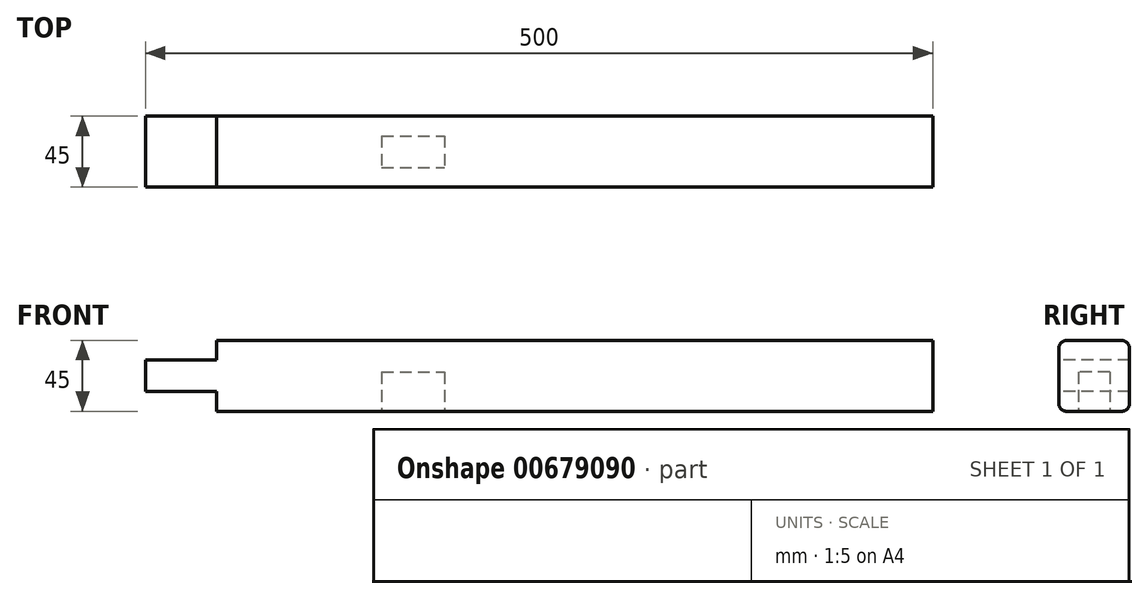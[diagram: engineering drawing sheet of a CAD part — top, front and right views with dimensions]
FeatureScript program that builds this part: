
annotation { "Feature Type Name" : "Feature", "Feature Type Description" : "" }
export const myFeature = defineFeature(function(context is Context, id is Id, definition is map)
    precondition{}
    {
        {
            var Q0;
            Q0=qCreatedBy(makeId("Right.planeOp"),FACE);
            var sketch = newSketch(context, id + "F0", { "sketchPlane" : qUnion([Q0])});
            skLineSegment(sketch, "E0.bottom", {"start": v(0, 0) * mm, "end": v(45, 0) * mm});
            skLineSegment(sketch, "E0.top", {"start": v(0, 45) * mm, "end": v(45, 45) * mm});
            skLineSegment(sketch, "E0.left", {"start": v(0, 0) * mm, "end": v(0, 45) * mm});
            skLineSegment(sketch, "E0.right", {"start": v(45, 0) * mm, "end": v(45, 45) * mm});
            skSolve(sketch);
        }
        {
            var Q0;
            Q0=qSketchRegion(id+"F0",true);
            extrude(context, id + "F1", {"entities" : qUnion([Q0]), "endBound" : BoundingType.SYMMETRIC, "depth" : 500 * mm, "offsetDistance" : 25 * mm});
        }
        {
            var Q0;
            Q0=makeQuery(id+"F1.opExtrude","SWEPT_EDGE",EDGE,{"disambiguationData":[OSD([sQuery(id+"F0.wireOp",EDGE,"E0.top"),sQuery(id+"F0.wireOp",EDGE,"E0.left")])]});
            var Q1;
            Q1=makeQuery(id+"F1.opExtrude","SWEPT_EDGE",EDGE,{"disambiguationData":[OSD([sQuery(id+"F0.wireOp",EDGE,"E0.top"),sQuery(id+"F0.wireOp",EDGE,"E0.right")])]});
            var Q2;
            Q2=makeQuery(id+"F1.opExtrude","SWEPT_EDGE",EDGE,{"disambiguationData":[OSD([sQuery(id+"F0.wireOp",EDGE,"E0.bottom"),sQuery(id+"F0.wireOp",EDGE,"E0.left")])]});
            var Q3;
            Q3=makeQuery(id+"F1.opExtrude","SWEPT_EDGE",EDGE,{"disambiguationData":[OSD([sQuery(id+"F0.wireOp",EDGE,"E0.bottom"),sQuery(id+"F0.wireOp",EDGE,"E0.right")])]});
            fillet(context, id + "F2", {"entities" : qUnion([Q0, Q1, Q2, Q3]), "radius" : 5 * mm, "tangentPropagation" : true, "allowEdgeOverflow" : false});
        }
        {
            var Q0;
            Q0=makeQuery(id+"F1.opExtrude","SWEPT_FACE",FACE,{"disambiguationData":[OSD([sQuery(id+"F0.wireOp",EDGE,"E0.left")])]});
            var sketch = newSketch(context, id + "F3", { "sketchPlane" : qUnion([Q0])});
            skLineSegment(sketch, "E1", {"start": v(-250, 22.5) * mm, "end": v(-205, 22.5) * mm, "construction": true});
            skLineSegment(sketch, "E2.bottom", {"start": v(-205, 12.5) * mm, "end": v(-250, 12.5) * mm});
            skLineSegment(sketch, "E2.top", {"start": v(-205, 32.5) * mm, "end": v(-250, 32.5) * mm});
            skLineSegment(sketch, "E2.left", {"start": v(-205, 12.5) * mm, "end": v(-205, 32.5) * mm, "construction": true});
            skLineSegment(sketch, "E2.right", {"start": v(-250, 12.5) * mm, "end": v(-250, 32.5) * mm});
            skPoint(sketch, "E2.middle", {"position": v(-227.5, 22.5) * mm});
            skLineSegment(sketch, "E3.bottom", {"start": v(-250, 32.5) * mm, "end": v(-205, 32.5) * mm});
            skLineSegment(sketch, "E3.top", {"start": v(-250, 45) * mm, "end": v(-205, 45) * mm});
            skLineSegment(sketch, "E3.left", {"start": v(-250, 32.5) * mm, "end": v(-250, 45) * mm});
            skLineSegment(sketch, "E3.right", {"start": v(-205, 32.5) * mm, "end": v(-205, 45) * mm});
            skLineSegment(sketch, "E4.bottom", {"start": v(-250, 12.5) * mm, "end": v(-205, 12.5) * mm});
            skLineSegment(sketch, "E4.top", {"start": v(-250, 0) * mm, "end": v(-205, 0) * mm});
            skLineSegment(sketch, "E4.left", {"start": v(-250, 12.5) * mm, "end": v(-250, 0) * mm});
            skLineSegment(sketch, "E4.right", {"start": v(-205, 12.5) * mm, "end": v(-205, 0) * mm});
            skSolve(sketch);
        }
        {
            var Q0;
            Q0=qSketchRegion(id+"F3",true);
            extrude(context, id + "F4", {"entities" : qUnion([Q0]), "operationType" : NewBodyOperationType.REMOVE, "endBound" : BoundingType.THROUGH_ALL, "oppositeDirection" : true, "depth" : 25 * mm, "offsetDistance" : 25 * mm});
        }
        {
            var Q0;
            Q0=makeQuery(id+"F1.opExtrude","CAP_FACE",FACE,{"disambiguationData":[OSD([sQuery(id+"F0.wireOp",EDGE,"E0.bottom"),sQuery(id+"F0.wireOp",EDGE,"E0.top"),sQuery(id+"F0.wireOp",EDGE,"E0.left"),sQuery(id+"F0.wireOp",EDGE,"E0.right")])],"isStart":true});
            var sketch = newSketch(context, id + "F5", { "sketchPlane" : qUnion([Q0])});
            skLineSegment(sketch, "E5.bottom", {"start": v(130, 32.5) * mm, "end": v(170, 32.5) * mm});
            skLineSegment(sketch, "E5.top", {"start": v(130, 12.5) * mm, "end": v(170, 12.5) * mm});
            skLineSegment(sketch, "E5.left", {"start": v(130, 32.5) * mm, "end": v(130, 12.5) * mm});
            skLineSegment(sketch, "E5.right", {"start": v(170, 32.5) * mm, "end": v(170, 12.5) * mm});
            skPoint(sketch, "E5.middle", {"position": v(150, 22.5) * mm});
            skPoint(sketch, "E5.middle.positionSnap0", {"position": v(0, 22.5) * mm});
            skPoint(sketch, "E5.centerSnap0", {"position": v(0, 22.5) * mm});
            skSolve(sketch);
        }
        {
            var Q0;
            Q0=qSketchRegion(id+"F5",true);
            extrude(context, id + "F6", {"entities" : qUnion([Q0]), "operationType" : NewBodyOperationType.REMOVE, "oppositeDirection" : true, "depth" : 25 * mm, "offsetDistance" : 25 * mm});
        }
        {
            var Q0;
            Q0=makeQuery(id+"F1.opExtrude","SWEPT_FACE",FACE,{"disambiguationData":[OSD([sQuery(id+"F0.wireOp",EDGE,"E0.bottom")])]});
            var sketch = newSketch(context, id + "F7", { "sketchPlane" : qUnion([Q0])});
            skLineSegment(sketch, "E6.bottom", {"start": v(-100, -32.5) * mm, "end": v(-60, -32.5) * mm});
            skLineSegment(sketch, "E6.top", {"start": v(-100, -12.5) * mm, "end": v(-60, -12.5) * mm});
            skLineSegment(sketch, "E6.left", {"start": v(-100, -32.5) * mm, "end": v(-100, -12.5) * mm});
            skLineSegment(sketch, "E6.right", {"start": v(-60, -32.5) * mm, "end": v(-60, -12.5) * mm});
            skPoint(sketch, "E6.middle", {"position": v(-80, -22.5) * mm});
            skPoint(sketch, "E6.middle.positionSnap0", {"position": v(-205, -22.5) * mm});
            skPoint(sketch, "E6.centerSnap0", {"position": v(-205, -22.5) * mm});
            skSolve(sketch);
        }
        {
            var Q0;
            Q0 = qSketchRegion(id + "F7", true);
            extrude(context, id + "F8", {"entities" : qUnion([Q0]), "operationType" : NewBodyOperationType.REMOVE, "oppositeDirection" : true, "depth" : 25 * mm, "offsetDistance" : 25 * mm});
        }
    });
